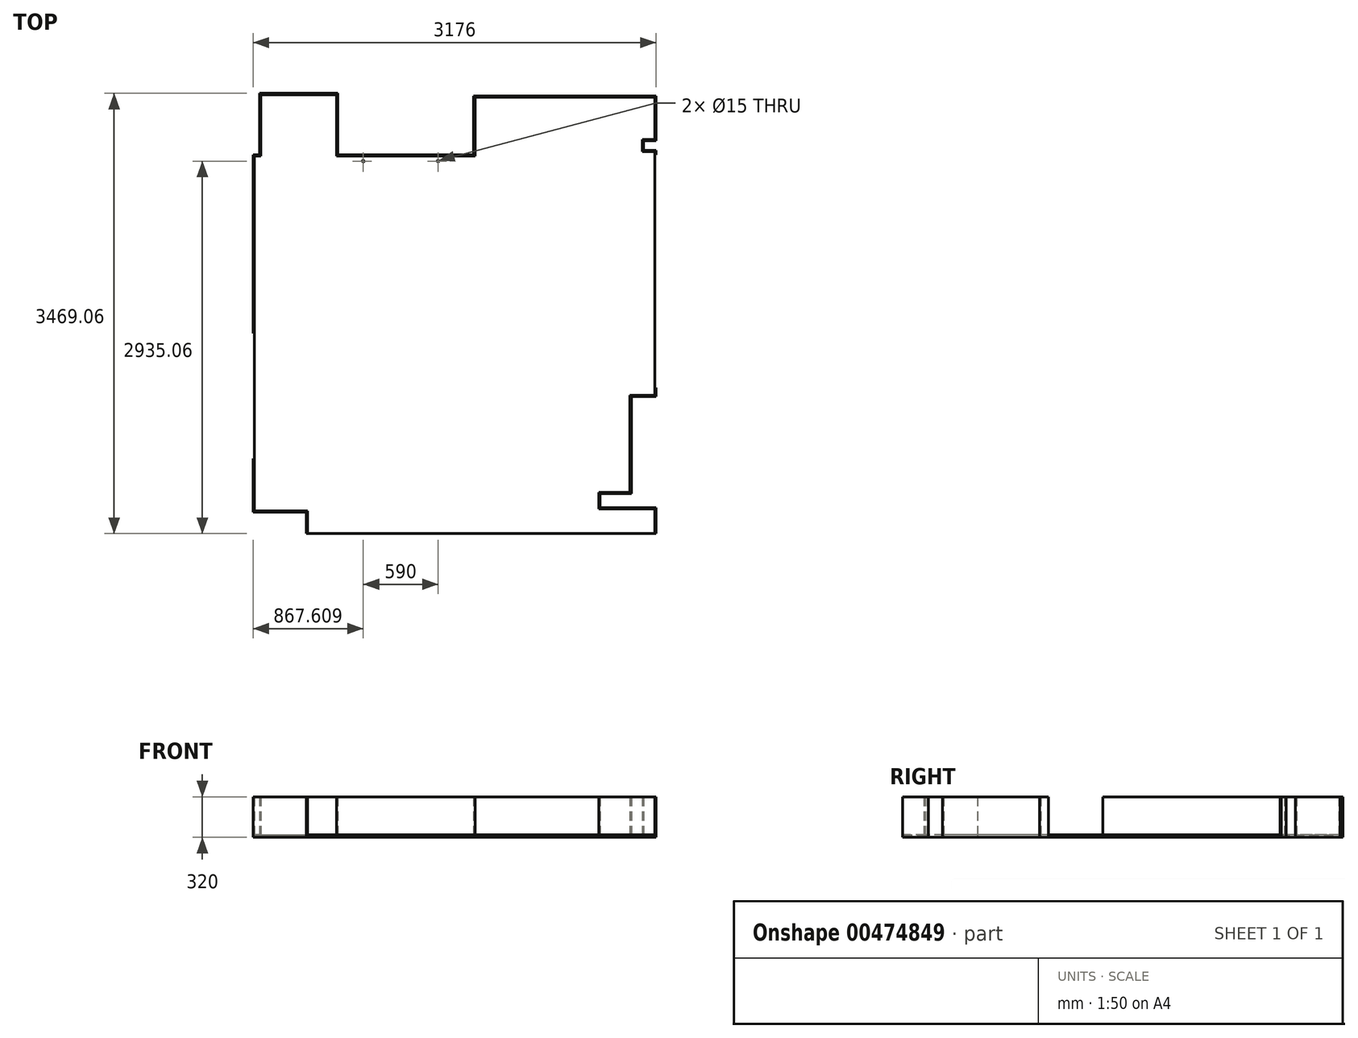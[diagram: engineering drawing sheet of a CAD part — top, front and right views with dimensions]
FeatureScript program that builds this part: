
annotation { "Feature Type Name" : "Feature", "Feature Type Description" : "" }
export const myFeature = defineFeature(function(context is Context, id is Id, definition is map)
    precondition{}
    {
        {
            var Q0;
            Q0=qCreatedBy(makeId("Top.planeOp"),FACE);
            var sketch = newSketch(context, id + "F0", { "sketchPlane" : qUnion([Q0])});
            skLineSegment(sketch, "E0", {"start": v(-1688, 1216.28) * mm, "end": v(-1091, 1216.28) * mm});
            skLineSegment(sketch, "E1", {"start": v(-1091, 1216.28) * mm, "end": v(-1091, 732.28) * mm});
            skLineSegment(sketch, "E2", {"start": v(-1091, 732.28) * mm, "end": v(0, 732.28) * mm});
            skLineSegment(sketch, "E3", {"start": v(0, 732.28) * mm, "end": v(0, 1195.28) * mm});
            skLineSegment(sketch, "E4", {"start": v(0, 1195.28) * mm, "end": v(1418, 1195.28) * mm});
            skLineSegment(sketch, "E5", {"start": v(1418, 1195.28) * mm, "end": v(1418, 863.28) * mm});
            skLineSegment(sketch, "E6", {"start": v(1418, 863.28) * mm, "end": v(1318.35, 863.28) * mm});
            skLineSegment(sketch, "E7", {"start": v(1318.35, 863.28) * mm, "end": v(1318.35, 768.28) * mm});
            skLineSegment(sketch, "E8", {"start": v(1318.35, 768.28) * mm, "end": v(1418, 768.28) * mm});
            skLineSegment(sketch, "E9", {"start": v(1418, 768.28) * mm, "end": v(1418, 662.28) * mm});
            skLineSegment(sketch, "E10", {"start": v(-1688, 1216.28) * mm, "end": v(-1688, 732.28) * mm});
            skLineSegment(sketch, "E11", {"start": v(-1688, 732.28) * mm, "end": v(-1738, 732.28) * mm});
            skLineSegment(sketch, "E12", {"start": v(-1738, 732.28) * mm, "end": v(-1738, -728.72) * mm});
            skLineSegment(sketch, "E13", {"start": v(1418, 662.28) * mm, "end": v(1418, -1153.72) * mm});
            skLineSegment(sketch, "E14", {"start": v(1418, -1153.72) * mm, "end": v(1418, -1153.72) * mm});
            skLineSegment(sketch, "E15", {"start": v(1418, -1153.72) * mm, "end": v(1221.85, -1153.72) * mm});
            skLineSegment(sketch, "E16", {"start": v(1221.85, -1153.72) * mm, "end": v(1221.85, -1917.72) * mm});
            skLineSegment(sketch, "E17", {"start": v(1221.85, -1917.72) * mm, "end": v(975.94, -1917.72) * mm});
            skLineSegment(sketch, "E18", {"start": v(975.94, -1917.72) * mm, "end": v(975.94, -2049.72) * mm});
            skLineSegment(sketch, "E19", {"start": v(975.94, -2049.72) * mm, "end": v(1418, -2049.72) * mm});
            skLineSegment(sketch, "E20", {"start": v(-1738, -728.72) * mm, "end": v(-1738, -2063.51) * mm});
            skLineSegment(sketch, "E21", {"start": v(-1738, -2063.51) * mm, "end": v(-1319.51, -2063.51) * mm});
            skLineSegment(sketch, "E22", {"start": v(-1319.51, -2063.51) * mm, "end": v(-1319.51, -2242.78) * mm});
            skLineSegment(sketch, "E23", {"start": v(-1319.51, -2242.78) * mm, "end": v(1418, -2242.78) * mm});
            skLineSegment(sketch, "E24", {"start": v(1418, -2242.78) * mm, "end": v(1418, -2049.72) * mm});
            skSolve(sketch);
        }
        {
            var Q0;
            Q0=qSketchRegion(id+"F0",true);
            extrude(context, id + "F1", {"entities" : qUnion([Q0]), "depth" : 20 * mm});
        }
        {
            var Q0;
            Q0=makeQuery(id+"F1.opExtrude","CAP_FACE",FACE,{"disambiguationData":[OSD([sQuery(id+"F0.wireOp",EDGE,"E0"),sQuery(id+"F0.wireOp",EDGE,"E1"),sQuery(id+"F0.wireOp",EDGE,"E2"),sQuery(id+"F0.wireOp",EDGE,"E3"),sQuery(id+"F0.wireOp",EDGE,"E4"),sQuery(id+"F0.wireOp",EDGE,"E5"),sQuery(id+"F0.wireOp",EDGE,"E6"),sQuery(id+"F0.wireOp",EDGE,"E7"),sQuery(id+"F0.wireOp",EDGE,"E8"),sQuery(id+"F0.wireOp",EDGE,"E9"),sQuery(id+"F0.wireOp",EDGE,"E10"),sQuery(id+"F0.wireOp",EDGE,"E11"),sQuery(id+"F0.wireOp",EDGE,"E12"),sQuery(id+"F0.wireOp",EDGE,"E13"),sQuery(id+"F0.wireOp",EDGE,"E15"),sQuery(id+"F0.wireOp",EDGE,"E16"),sQuery(id+"F0.wireOp",EDGE,"E17"),sQuery(id+"F0.wireOp",EDGE,"E18"),sQuery(id+"F0.wireOp",EDGE,"E19"),sQuery(id+"F0.wireOp",EDGE,"E20"),sQuery(id+"F0.wireOp",EDGE,"E21"),sQuery(id+"F0.wireOp",EDGE,"E22"),sQuery(id+"F0.wireOp",EDGE,"E23"),sQuery(id+"F0.wireOp",EDGE,"E24")])],"isStart":false});
            var sketch = newSketch(context, id + "F2", { "sketchPlane" : qUnion([Q0])});
            skLineSegment(sketch, "E25", {"start": v(-1738, 732.28) * mm, "end": v(-1688, 732.28) * mm});
            skLineSegment(sketch, "E26", {"start": v(-1688, 732.28) * mm, "end": v(-1688, 1216.28) * mm});
            skLineSegment(sketch, "E27", {"start": v(-1688, 1216.28) * mm, "end": v(-1091, 1216.28) * mm});
            skLineSegment(sketch, "E28", {"start": v(-1091, 1216.28) * mm, "end": v(-1091, 732.28) * mm});
            skLineSegment(sketch, "E29", {"start": v(-1091, 732.28) * mm, "end": v(0, 732.28) * mm});
            skLineSegment(sketch, "E30", {"start": v(0, 732.28) * mm, "end": v(0, 1195.28) * mm});
            skLineSegment(sketch, "E31", {"start": v(0, 1195.28) * mm, "end": v(1418, 1195.28) * mm});
            skLineSegment(sketch, "E32", {"start": v(1418, 1195.28) * mm, "end": v(1418, 863.28) * mm});
            skLineSegment(sketch, "E33", {"start": v(1418, 863.28) * mm, "end": v(1318.35, 863.28) * mm});
            skLineSegment(sketch, "E34", {"start": v(1318.35, 863.28) * mm, "end": v(1318.35, 768.28) * mm});
            skLineSegment(sketch, "E35", {"start": v(1318.35, 768.28) * mm, "end": v(1418, 768.28) * mm});
            skLineSegment(sketch, "E36", {"start": v(1418, 768.28) * mm, "end": v(1418, 741.5) * mm});
            skLineSegment(sketch, "E37", {"start": v(1418, -1153.72) * mm, "end": v(1221.85, -1153.72) * mm});
            skLineSegment(sketch, "E38", {"start": v(1221.85, -1153.72) * mm, "end": v(1221.85, -1917.72) * mm});
            skLineSegment(sketch, "E39", {"start": v(1221.85, -1917.72) * mm, "end": v(975.94, -1917.72) * mm});
            skLineSegment(sketch, "E40", {"start": v(975.94, -1917.72) * mm, "end": v(975.94, -2049.72) * mm});
            skLineSegment(sketch, "E41", {"start": v(975.94, -2049.72) * mm, "end": v(1418, -2049.72) * mm});
            skLineSegment(sketch, "E42", {"start": v(1418, -2049.72) * mm, "end": v(1418, -2242.78) * mm});
            skLineSegment(sketch, "E43", {"start": v(-1738, 732.28) * mm, "end": v(-1738, -665.62) * mm});
            skLineSegment(sketch, "E44.0", {"start": v(-1748, 742.28) * mm, "end": v(-1748, -665.62) * mm});
            skLineSegment(sketch, "E44.1", {"start": v(-1748, 742.28) * mm, "end": v(-1698, 742.28) * mm});
            skLineSegment(sketch, "E44.2", {"start": v(-1698, 742.28) * mm, "end": v(-1698, 1226.28) * mm});
            skLineSegment(sketch, "E44.3", {"start": v(-1698, 1226.28) * mm, "end": v(-1081, 1226.28) * mm});
            skLineSegment(sketch, "E44.4", {"start": v(-1081, 1226.28) * mm, "end": v(-1081, 742.28) * mm});
            skLineSegment(sketch, "E44.5", {"start": v(-1081, 742.28) * mm, "end": v(-10, 742.28) * mm});
            skLineSegment(sketch, "E44.6", {"start": v(-10, 742.28) * mm, "end": v(-10, 1205.28) * mm});
            skLineSegment(sketch, "E44.7", {"start": v(-10, 1205.28) * mm, "end": v(1428, 1205.28) * mm});
            skLineSegment(sketch, "E44.8", {"start": v(1428, 1205.28) * mm, "end": v(1428, 853.28) * mm});
            skLineSegment(sketch, "E44.9", {"start": v(1231.85, -1927.72) * mm, "end": v(985.94, -1927.72) * mm});
            skLineSegment(sketch, "E44.10", {"start": v(985.94, -1927.72) * mm, "end": v(985.94, -2039.72) * mm});
            skLineSegment(sketch, "E44.11", {"start": v(985.94, -2039.72) * mm, "end": v(1428, -2039.72) * mm});
            skLineSegment(sketch, "E44.12", {"start": v(1428, -2039.72) * mm, "end": v(1428, -2242.78) * mm});
            skLineSegment(sketch, "E44.13", {"start": v(1231.85, -1163.72) * mm, "end": v(1231.85, -1927.72) * mm});
            skLineSegment(sketch, "E44.14", {"start": v(1428, -1163.72) * mm, "end": v(1231.85, -1163.72) * mm});
            skLineSegment(sketch, "E44.15", {"start": v(1428, 778.28) * mm, "end": v(1428, 741.5) * mm});
            skLineSegment(sketch, "E44.16", {"start": v(1328.35, 778.28) * mm, "end": v(1428, 778.28) * mm});
            skLineSegment(sketch, "E44.17", {"start": v(1328.35, 853.28) * mm, "end": v(1328.35, 778.28) * mm});
            skLineSegment(sketch, "E44.18", {"start": v(1428, 853.28) * mm, "end": v(1328.35, 853.28) * mm});
            skLineSegment(sketch, "E45", {"start": v(-1748, -665.62) * mm, "end": v(-1738, -665.62) * mm});
            skLineSegment(sketch, "E46", {"start": v(1428, -2242.78) * mm, "end": v(1418, -2242.78) * mm});
            skLineSegment(sketch, "E47", {"start": v(-1319.51, -2242.78) * mm, "end": v(-1319.51, -2063.51) * mm});
            skLineSegment(sketch, "E48", {"start": v(-1319.51, -2063.51) * mm, "end": v(-1738, -2063.51) * mm});
            skLineSegment(sketch, "E49", {"start": v(-1738, -2063.51) * mm, "end": v(-1738, -1652.2) * mm});
            skLineSegment(sketch, "E50.0", {"start": v(-1748, -2073.51) * mm, "end": v(-1748, -1652.2) * mm});
            skLineSegment(sketch, "E50.1", {"start": v(-1329.51, -2073.51) * mm, "end": v(-1748, -2073.51) * mm});
            skLineSegment(sketch, "E50.2", {"start": v(-1329.51, -2242.78) * mm, "end": v(-1329.51, -2073.51) * mm});
            skLineSegment(sketch, "E51", {"start": v(-1748, -1652.2) * mm, "end": v(-1738, -1652.2) * mm});
            skLineSegment(sketch, "E52", {"start": v(-1329.51, -2242.78) * mm, "end": v(-1319.51, -2242.78) * mm});
            skLineSegment(sketch, "E53", {"start": v(1418, 741.5) * mm, "end": v(1428, 741.5) * mm});
            skLineSegment(sketch, "E54", {"start": v(1418, -1092.47) * mm, "end": v(1428, -1092.47) * mm});
            skLineSegment(sketch, "E55.trimOffspring", {"start": v(1428, -1092.47) * mm, "end": v(1428, -1163.72) * mm});
            skLineSegment(sketch, "E56.trimOffspring", {"start": v(1418, -1092.47) * mm, "end": v(1418, -1153.72) * mm});
            skSolve(sketch);
        }
        {
            var Q0;
            Q0=makeQuery(id+"F2.imprint","IMPRINT",FACE,{"disambiguationData":[TD([[makeQuery(id+"F2.imprint","IMPRINT",EDGE,{"derivedFrom":sQuery(id+"F2.wireOp",EDGE,"E47")}),-1.0]])]});
            var Q1;
            Q1=makeQuery(id+"F2.imprint","IMPRINT",FACE,{"disambiguationData":[TD([[makeQuery(id+"F2.imprint","IMPRINT",EDGE,{"derivedFrom":sQuery(id+"F2.wireOp",EDGE,"E25")}),-1.0]])]});
            var Q2;
            Q2=makeQuery(id+"F2.imprint","IMPRINT",FACE,{"disambiguationData":[TD([[makeQuery(id+"F2.imprint","IMPRINT",EDGE,{"derivedFrom":sQuery(id+"F2.wireOp",EDGE,"E37")}),1.0]])]});
            extrude(context, id + "F3", {"entities" : qUnion([Q0, Q1, Q2]), "depth" : 300 * mm, "hasSecondDirection" : true, "secondDirectionOppositeDirection" : true, "secondDirectionDepth" : 20 * mm});
        }
        {
            var Q0;
            Q0=makeQuery(id+"F1.opExtrude","CAP_FACE",FACE,{"disambiguationData":[OSD([sQuery(id+"F0.wireOp",EDGE,"E0"),sQuery(id+"F0.wireOp",EDGE,"E1"),sQuery(id+"F0.wireOp",EDGE,"E2"),sQuery(id+"F0.wireOp",EDGE,"E3"),sQuery(id+"F0.wireOp",EDGE,"E4"),sQuery(id+"F0.wireOp",EDGE,"E5"),sQuery(id+"F0.wireOp",EDGE,"E6"),sQuery(id+"F0.wireOp",EDGE,"E7"),sQuery(id+"F0.wireOp",EDGE,"E8"),sQuery(id+"F0.wireOp",EDGE,"E9"),sQuery(id+"F0.wireOp",EDGE,"E10"),sQuery(id+"F0.wireOp",EDGE,"E11"),sQuery(id+"F0.wireOp",EDGE,"E12"),sQuery(id+"F0.wireOp",EDGE,"E13"),sQuery(id+"F0.wireOp",EDGE,"E15"),sQuery(id+"F0.wireOp",EDGE,"E16"),sQuery(id+"F0.wireOp",EDGE,"E17"),sQuery(id+"F0.wireOp",EDGE,"E18"),sQuery(id+"F0.wireOp",EDGE,"E19"),sQuery(id+"F0.wireOp",EDGE,"E20"),sQuery(id+"F0.wireOp",EDGE,"E21"),sQuery(id+"F0.wireOp",EDGE,"E22"),sQuery(id+"F0.wireOp",EDGE,"E23"),sQuery(id+"F0.wireOp",EDGE,"E24")])],"isStart":false});
            var sketch = newSketch(context, id + "F4", { "sketchPlane" : qUnion([Q0])});
            skCircle(sketch, "E57", {"center": v(-880.4, 692.28) * mm, "radius": 7.5 * mm});
            skCircle(sketch, "E58", {"center": v(-290.4, 692.28) * mm, "radius": 7.5 * mm});
            skSolve(sketch);
        }
        {
            var Q0;
            Q0=makeQuery(id+"F4.imprint","IMPRINT",FACE,{"disambiguationData":[TD([[makeQuery(id+"F4.imprint","IMPRINT",EDGE,{"derivedFrom":sQuery(id+"F4.wireOp",EDGE,"E57")}),1.0]])]});
            var Q1;
            Q1=makeQuery(id+"F4.imprint","IMPRINT",FACE,{"disambiguationData":[TD([[makeQuery(id+"F4.imprint","IMPRINT",EDGE,{"derivedFrom":sQuery(id+"F4.wireOp",EDGE,"E58")}),1.0]])]});
            extrude(context, id + "F5", {"entities" : qUnion([Q0, Q1]), "operationType" : NewBodyOperationType.REMOVE, "oppositeDirection" : true, "depth" : 25 * mm});
        }
    });
